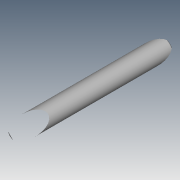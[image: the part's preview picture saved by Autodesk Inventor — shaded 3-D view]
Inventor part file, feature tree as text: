
AUTODESK INVENTOR PART (.ipt)
format: ipt  version: 2015 (Build 190159000, 159)  size: 69,120 bytes
history: native  units: mm
features: extrude x1, sketch x1
ambient origin geometry x8: Origin, YZ Plane, XZ Plane, XY Plane, X Axis, Y Axis, Z Axis, Center Point
bodies: Solid1 (feature_tree)
feature tree (2):
  extrude  "Extrusion1"  Depth=80.0mm TaperAngle=0.0deg
  sketch  "Sketch1"  dims[d0=10.0mm d1=80.0mm d2=0.0mm]
